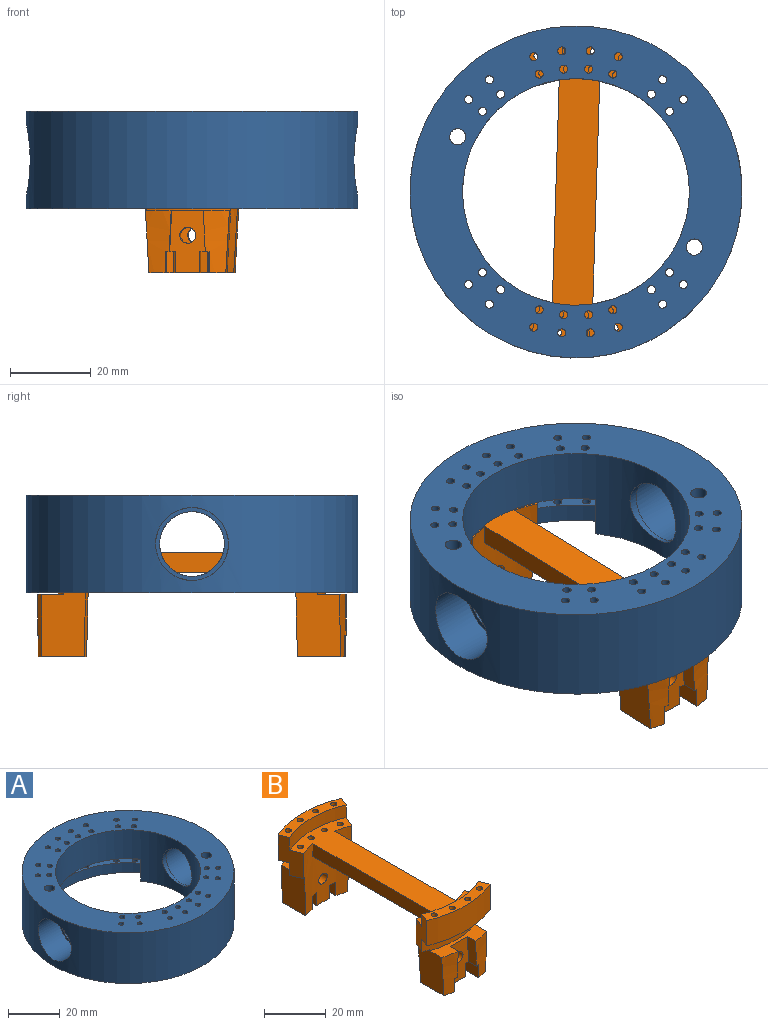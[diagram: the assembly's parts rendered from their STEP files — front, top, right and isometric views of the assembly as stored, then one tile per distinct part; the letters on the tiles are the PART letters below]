
ASSEMBLY  parts=2 mates=1
PART A: 80 faces, bbox 82x82x24 mm
  f0: plane 82x82mm, normal (0,0,-1), area 1952.1mm2, adj f9,f11,f14,f15,f22,f24,f26,f28
  f1: plane 82x82mm, normal (0,0,1), area 2692.3mm2, adj f9,f11,f12,f13,f40,f41,f42,f43
  f2: plane 53.41x16.54mm, normal (0,0,-1), area 242.5mm2, adj f9,f21,f22,f24,f72,f73,f74,f75
  f3: plane 54.06x17.34mm, normal (0,0,-1), area 267.8mm2, adj f8,f9,f25,f26,f28,f29,f64,f65
  f4: plane 61.27x18.7mm, normal (0,0,-1), area 297.4mm2, adj f21,f22,f23,f24,f56,f57,f58,f59
  f5: plane 61.27x18.24mm, normal (0,0,1), area 246.7mm2, adj f22,f23,f24,f31,f48,f49,f50,f51
  f6: plane 61.27x18.7mm, normal (0,0,-1), area 272.1mm2, adj f8,f25,f26,f27,f28,f29,f40,f41
  f7: plane 61.27x18.24mm, normal (0,0,1), area 246.7mm2, adj f26,f27,f28,f30,f32,f33,f34,f35
  f8: cylinder r=33.4mm len=27.36mm, axis (0,0,-1), area 160.3mm2, adj f3,f6,f25,f26
  f9: cylinder r=28mm len=56mm, axis (0,0,-1), area 2687.3mm2, adj f0,f1,f2,f3,f10,f14,f15,f16
  f10: cylinder r=8mm len=16mm, axis (-1,0,0), area 79.4mm2, adj f9,f18
  f11: cylinder r=41mm len=82mm, axis (0,0,-1), area 5671.2mm2, adj f0,f1,f17,f19
  f12: cylinder r=2mm len=20.5mm, axis (0,0,-1), area 257.6mm2, adj f1,f14
  f13: cylinder r=2mm len=20.5mm, axis (0,0,-1), area 257.6mm2, adj f1,f15
  f14: cone r=5.5mm half-angle=45deg, axis (0,0,-1), area 108.8mm2, adj f0,f9,f12
  f15: cone r=2mm half-angle=45deg, axis (0,0,-1), area 108.8mm2, adj f0,f9,f13
  f16: cylinder r=8mm len=16mm, axis (-1,0,0), area 79.5mm2, adj f9,f20
  f17: cylinder r=9mm len=18mm, axis (-1,0,0), area 650.4mm2, adj f11,f18
  f18: plane 18x18mm, normal (1,0,0), area 53.4mm2, adj f10,f17
  f19: cylinder r=9mm len=18mm, axis (1,0,0), area 650.4mm2, adj f11,f20
  f20: plane 18x18mm, normal (-1,0,0), area 53.4mm2, adj f16,f19
  f21: cylinder r=32.6mm len=53.41mm, axis (0,0,-1), area 312.9mm2, adj f2,f4,f22,f24
  f22: plane 15.4x7.7mm, normal (-0.57,0.82,0), area 103.4mm2, adj f0,f2,f4,f5,f9,f21,f23,f31
  f23: cylinder r=37.4mm len=61.27mm, axis (0,0,-1), area 775.5mm2, adj f4,f5,f22,f24
  f24: plane 15.4x7.7mm, normal (0.57,0.82,0), area 103.4mm2, adj f0,f2,f4,f5,f9,f21,f23,f31
  f25: plane 5x0.8mm, normal (1,0,0), area 4mm2, adj f3,f6,f8,f29
  f26: plane 15.4x7.7mm, normal (0.57,-0.82,0), area 99.4mm2, adj f0,f3,f6,f7,f8,f9,f27,f30
  f27: cylinder r=37.4mm len=61.27mm, axis (0,0,-1), area 775.5mm2, adj f6,f7,f26,f28
  f28: plane 15.4x7.7mm, normal (-0.57,-0.82,0), area 103.4mm2, adj f0,f3,f6,f7,f9,f27,f29,f30
  f29: cylinder r=32.6mm len=26.7mm, axis (0,0,-1), area 156.5mm2, adj f3,f6,f25,f28
  f30: cylinder r=33.4mm len=54.72mm, axis (0,0,-1), area 295mm2, adj f0,f7,f26,f28
  f31: cylinder r=33.4mm len=54.72mm, axis (0,0,-1), area 295mm2, adj f0,f5,f22,f24
  f32: cylinder r=1mm len=4.6mm, axis (0,0,-1), area 28.9mm2, adj f0,f7
  f33: cylinder r=1mm len=4.6mm, axis (0,0,-1), area 28.9mm2, adj f0,f7
  f34: cylinder r=1mm len=4.6mm, axis (0,0,-1), area 28.9mm2, adj f0,f7
  f35: cylinder r=1mm len=4.6mm, axis (0,0,-1), area 28.9mm2, adj f0,f7
  f36: cylinder r=1mm len=4.6mm, axis (0,0,-1), area 28.9mm2, adj f0,f7
  f37: cylinder r=1mm len=4.6mm, axis (0,0,-1), area 28.9mm2, adj f0,f7
  f38: cylinder r=1mm len=4.6mm, axis (0,0,-1), area 28.9mm2, adj f0,f7
  f39: cylinder r=1mm len=4.6mm, axis (0,0,-1), area 28.9mm2, adj f0,f7
  f40: cylinder r=1mm len=8.6mm, axis (0,0,-1), area 54mm2, adj f1,f6
  f41: cylinder r=1mm len=8.6mm, axis (0,0,-1), area 54mm2, adj f1,f6
  f42: cylinder r=1mm len=8.6mm, axis (0,0,-1), area 54mm2, adj f1,f6
  f43: cylinder r=1mm len=8.6mm, axis (0,0,-1), area 54mm2, adj f1,f6
  f44: cylinder r=1mm len=8.6mm, axis (0,0,-1), area 54mm2, adj f1,f6
  f45: cylinder r=1mm len=8.6mm, axis (0,0,-1), area 54mm2, adj f1,f6
  f46: cylinder r=1mm len=8.6mm, axis (0,0,-1), area 54mm2, adj f1,f6
  f47: cylinder r=1mm len=8.6mm, axis (0,0,-1), area 54mm2, adj f1,f6
  f48: cylinder r=1mm len=4.6mm, axis (0,0,-1), area 28.9mm2, adj f0,f5
  f49: cylinder r=1mm len=4.6mm, axis (0,0,-1), area 28.9mm2, adj f0,f5
  f50: cylinder r=1mm len=4.6mm, axis (0,0,-1), area 28.9mm2, adj f0,f5
  f51: cylinder r=1mm len=4.6mm, axis (0,0,-1), area 28.9mm2, adj f0,f5
  f52: cylinder r=1mm len=4.6mm, axis (0,0,-1), area 28.9mm2, adj f0,f5
  f53: cylinder r=1mm len=4.6mm, axis (0,0,-1), area 28.9mm2, adj f0,f5
  f54: cylinder r=1mm len=4.6mm, axis (0,0,-1), area 28.9mm2, adj f0,f5
  f55: cylinder r=1mm len=4.6mm, axis (0,0,-1), area 28.9mm2, adj f0,f5
  f56: cylinder r=1mm len=8.6mm, axis (0,0,-1), area 54mm2, adj f1,f4
  f57: cylinder r=1mm len=8.6mm, axis (0,0,-1), area 54mm2, adj f1,f4
  f58: cylinder r=1mm len=8.6mm, axis (0,0,-1), area 54mm2, adj f1,f4
  f59: cylinder r=1mm len=8.6mm, axis (0,0,-1), area 54mm2, adj f1,f4
  f60: cylinder r=1mm len=8.6mm, axis (0,0,-1), area 54mm2, adj f1,f4
  f61: cylinder r=1mm len=8.6mm, axis (0,0,-1), area 54mm2, adj f1,f4
  f62: cylinder r=1mm len=8.6mm, axis (0,0,-1), area 54mm2, adj f1,f4
  f63: cylinder r=1mm len=8.6mm, axis (0,0,-1), area 54mm2, adj f1,f4
  f64: cylinder r=1mm len=13.6mm, axis (0,0,-1), area 85.5mm2, adj f1,f3
  f65: cylinder r=1mm len=13.6mm, axis (0,0,-1), area 85.5mm2, adj f1,f3
  f66: cylinder r=1mm len=13.6mm, axis (0,0,-1), area 85.5mm2, adj f1,f3
  f67: cylinder r=1mm len=13.6mm, axis (0,0,-1), area 85.5mm2, adj f1,f3
  f68: cylinder r=1mm len=13.6mm, axis (0,0,-1), area 85.5mm2, adj f1,f3
  f69: cylinder r=1mm len=13.6mm, axis (0,0,-1), area 85.5mm2, adj f1,f3
  f70: cylinder r=1mm len=13.6mm, axis (0,0,-1), area 85.5mm2, adj f1,f3
  f71: cylinder r=1mm len=13.6mm, axis (0,0,-1), area 85.5mm2, adj f1,f3
  f72: cylinder r=1mm len=13.6mm, axis (0,0,-1), area 85.5mm2, adj f1,f2
  f73: cylinder r=1mm len=13.6mm, axis (0,0,-1), area 85.5mm2, adj f1,f2
  f74: cylinder r=1mm len=13.6mm, axis (0,0,-1), area 85.5mm2, adj f1,f2
  f75: cylinder r=1mm len=13.6mm, axis (0,0,-1), area 85.5mm2, adj f1,f2
  f76: cylinder r=1mm len=13.6mm, axis (0,0,-1), area 85.5mm2, adj f1,f2
  f77: cylinder r=1mm len=13.6mm, axis (0,0,-1), area 85.5mm2, adj f1,f2
  f78: cylinder r=1mm len=13.6mm, axis (0,0,-1), area 85.5mm2, adj f1,f2
  f79: cylinder r=1mm len=13.6mm, axis (0,0,-1), area 85.5mm2, adj f1,f2
PART B: 84 faces, bbox 29.1x76x30.8 mm
  f0: cylinder r=28mm len=25.8mm, axis (0,0,1), area 459.5mm2, adj f3,f4,f7,f8,f9,f12,f16,f17
  f1: plane 29.07x6.65mm, normal (0,0,1), area 100.5mm2, adj f4,f12,f27,f28,f37,f38,f39,f40
  f2: plane 29.07x6.65mm, normal (0,0,-1), area 100.5mm2, adj f4,f10,f12,f27,f37,f38,f39,f40
  f3: plane 66x25.93mm, normal (0,0,1), area 778.2mm2, adj f0,f4,f12,f28,f29,f31,f33,f35
  f4: plane 15x8.28mm, normal (-0.92,0.39,0), area 90mm2, adj f0,f1,f2,f3,f10,f18,f27,f28
  f5: plane 20.75x6.67mm, normal (0,0,1), area 78.7mm2, adj f6,f10,f11,f13,f14,f15,f17,f19
  f6: cylinder r=38.2mm len=15.4mm, axis (0,0,1), area 83.4mm2, adj f5,f7,f14,f19,f21,f22
  f7: plane 11.47x4.05mm, normal (0,0,-1), area 42.5mm2, adj f0,f6,f19,f22
  f8: plane 11.47x4.05mm, normal (0,0,-1), area 42.5mm2, adj f0,f11,f17,f25
  f9: plane 6.41x6mm, normal (0,0,-1), area 37.8mm2, adj f0,f15,f20,f23
  f10: cylinder r=33mm len=25.93mm, axis (0,0,1), area 141.7mm2, adj f2,f4,f5,f12,f16,f17,f18,f19
  f11: cylinder r=38.2mm len=15.4mm, axis (0,0,1), area 83.4mm2, adj f5,f8,f13,f17,f24,f25
  f12: plane 15x8.28mm, normal (0.92,0.39,0), area 90mm2, adj f0,f1,f2,f3,f10,f16,f27,f28
  f13: plane 10.2x3.75mm, normal (-1,0,-0.05), area 38mm2, adj f5,f11,f15,f24
  f14: plane 10.2x3.75mm, normal (1,0,-0.05), area 38mm2, adj f5,f6,f15,f21
  f15: plane 15.4x8.9mm, normal (0,-1,0), area 105.1mm2, adj f5,f9,f13,f14,f20,f21,f23,f24
  f16: plane 5.57x2.56mm, normal (0,0,-1), area 8.5mm2, adj f0,f10,f12,f17
  f17: plane 15.82x11.03mm, normal (1,0,-0.06), area 167.3mm2, adj f0,f5,f8,f10,f11,f16
  f18: plane 5.57x2.56mm, normal (0,0,-1), area 8.5mm2, adj f0,f4,f10,f19
  f19: plane 15.82x11.03mm, normal (-1,0,-0.06), area 167.3mm2, adj f0,f5,f6,f7,f10,f18
  f20: plane 6.41x5.2mm, normal (-1,0,0), area 33.3mm2, adj f0,f9,f15,f21
  f21: plane 10.48x2.45mm, normal (0,0,-1), area 19.7mm2, adj f0,f6,f14,f15,f20,f22
  f22: plane 10.34x5.2mm, normal (1,0,0), area 53.8mm2, adj f0,f6,f7,f21
  f23: plane 6.41x5.2mm, normal (1,0,0), area 33.3mm2, adj f0,f9,f15,f24
  f24: plane 10.48x2.45mm, normal (0,0,-1), area 19.7mm2, adj f0,f11,f13,f15,f23,f25
  f25: plane 10.34x5.2mm, normal (-1,0,0), area 53.8mm2, adj f0,f8,f11,f24
  f26: cylinder r=1.95mm len=6.32mm, axis (0,1,0), area 77mm2, adj f0,f15
  f27: cylinder r=37mm len=29.07mm, axis (0,0,-1), area 298.8mm2, adj f1,f2,f4,f12
  f28: cylinder r=33mm len=25.93mm, axis (0,0,-1), area 133.2mm2, adj f1,f3,f4,f12
  f29: cylinder r=1mm len=10mm, axis (0,0,-1), area 62.8mm2, adj f3,f30
  f30: plane 2x2mm, normal (0,0,1), area 3.1mm2, adj f29
  f31: cylinder r=1mm len=10mm, axis (0,0,-1), area 62.8mm2, adj f3,f32
  f32: plane 2x2mm, normal (0,0,1), area 3.1mm2, adj f31
  f33: cylinder r=1mm len=10mm, axis (0,0,-1), area 62.8mm2, adj f3,f34
  f34: plane 2x2mm, normal (0,0,1), area 3.1mm2, adj f33
  f35: cylinder r=1mm len=10mm, axis (0,0,-1), area 62.8mm2, adj f3,f36
  f36: plane 2x2mm, normal (0,0,1), area 3.1mm2, adj f35
  f37: cylinder r=1mm len=10mm, axis (0,0,-1), area 62.8mm2, adj f1,f2
  f38: cylinder r=1mm len=10mm, axis (0,0,-1), area 62.8mm2, adj f1,f2
  f39: cylinder r=1mm len=10mm, axis (0,0,-1), area 62.8mm2, adj f1,f2
  f40: cylinder r=1mm len=10mm, axis (0,0,-1), area 62.8mm2, adj f1,f2
  f41: plane 55.1x5mm, normal (-1,0,0), area 275.5mm2, adj f0,f3,f43,f44
  f42: plane 55.1x5mm, normal (1,0,0), area 275.5mm2, adj f0,f3,f43,f44
  f43: plane 56x10mm, normal (0,0,-1), area 557mm2, adj f0,f41,f42,f44
  f44: cylinder r=28mm len=25.8mm, axis (0,0,1), area 459.5mm2, adj f3,f41,f42,f43,f47,f50,f51,f52
  f45: plane 29.07x6.65mm, normal (0,0,1), area 100.5mm2, adj f47,f55,f70,f71,f80,f81,f82,f83
  f46: plane 29.07x6.65mm, normal (0,0,-1), area 100.5mm2, adj f47,f53,f55,f70,f80,f81,f82,f83
  f47: plane 15x8.28mm, normal (-0.92,-0.39,0), area 90mm2, adj f3,f44,f45,f46,f53,f61,f70,f71
  f48: plane 20.75x6.67mm, normal (0,0,1), area 78.7mm2, adj f49,f53,f54,f56,f57,f58,f60,f62
  f49: cylinder r=38.2mm len=15.4mm, axis (0,0,1), area 83.4mm2, adj f48,f50,f57,f62,f64,f65
  f50: plane 11.47x4.05mm, normal (0,0,-1), area 42.5mm2, adj f44,f49,f62,f65
  f51: plane 11.47x4.05mm, normal (0,0,-1), area 42.5mm2, adj f44,f54,f60,f68
  f52: plane 6.41x6mm, normal (0,0,-1), area 37.8mm2, adj f44,f58,f63,f66
  f53: cylinder r=33mm len=25.93mm, axis (0,0,1), area 141.7mm2, adj f46,f47,f48,f55,f59,f60,f61,f62
  f54: cylinder r=38.2mm len=15.4mm, axis (0,0,1), area 83.4mm2, adj f48,f51,f56,f60,f67,f68
  f55: plane 15x8.28mm, normal (0.92,-0.39,0), area 90mm2, adj f3,f44,f45,f46,f53,f59,f70,f71
  f56: plane 10.2x3.75mm, normal (-1,0,-0.05), area 38mm2, adj f48,f54,f58,f67
  f57: plane 10.2x3.75mm, normal (1,0,-0.05), area 38mm2, adj f48,f49,f58,f64
  f58: plane 15.4x8.9mm, normal (0,1,0), area 105.1mm2, adj f48,f52,f56,f57,f63,f64,f66,f67
  f59: plane 5.57x2.56mm, normal (0,0,-1), area 8.5mm2, adj f44,f53,f55,f60
  f60: plane 15.82x11.03mm, normal (1,0,-0.06), area 167.3mm2, adj f44,f48,f51,f53,f54,f59
  f61: plane 5.57x2.56mm, normal (0,0,-1), area 8.5mm2, adj f44,f47,f53,f62
  f62: plane 15.82x11.03mm, normal (-1,0,-0.06), area 167.3mm2, adj f44,f48,f49,f50,f53,f61
  f63: plane 6.41x5.2mm, normal (-1,0,0), area 33.3mm2, adj f44,f52,f58,f64
  f64: plane 10.48x2.45mm, normal (0,0,-1), area 19.7mm2, adj f44,f49,f57,f58,f63,f65
  f65: plane 10.34x5.2mm, normal (1,0,0), area 53.8mm2, adj f44,f49,f50,f64
  f66: plane 6.41x5.2mm, normal (1,0,0), area 33.3mm2, adj f44,f52,f58,f67
  f67: plane 10.48x2.45mm, normal (0,0,-1), area 19.7mm2, adj f44,f54,f56,f58,f66,f68
  f68: plane 10.34x5.2mm, normal (-1,0,0), area 53.8mm2, adj f44,f51,f54,f67
  f69: cylinder r=1.95mm len=6.32mm, axis (0,-1,0), area 77mm2, adj f44,f58
  f70: cylinder r=37mm len=29.07mm, axis (0,0,-1), area 298.8mm2, adj f45,f46,f47,f55
  f71: cylinder r=33mm len=25.93mm, axis (0,0,-1), area 133.2mm2, adj f3,f45,f47,f55
  f72: cylinder r=1mm len=10mm, axis (0,0,-1), area 62.8mm2, adj f3,f73
  f73: plane 2x2mm, normal (0,0,1), area 3.1mm2, adj f72
  f74: cylinder r=1mm len=10mm, axis (0,0,-1), area 62.8mm2, adj f3,f75
  f75: plane 2x2mm, normal (0,0,1), area 3.1mm2, adj f74
  f76: cylinder r=1mm len=10mm, axis (0,0,-1), area 62.8mm2, adj f3,f77
  f77: plane 2x2mm, normal (0,0,1), area 3.1mm2, adj f76
  f78: cylinder r=1mm len=10mm, axis (0,0,-1), area 62.8mm2, adj f3,f79
  f79: plane 2x2mm, normal (0,0,1), area 3.1mm2, adj f78
  f80: cylinder r=1mm len=10mm, axis (0,0,-1), area 62.8mm2, adj f45,f46
  f81: cylinder r=1mm len=10mm, axis (0,0,-1), area 62.8mm2, adj f45,f46
  f82: cylinder r=1mm len=10mm, axis (0,0,-1), area 62.8mm2, adj f45,f46
  f83: cylinder r=1mm len=10mm, axis (0,0,-1), area 62.8mm2, adj f45,f46
PLACE A t=(0,0,-24)mm
PLACE B rot(axis=(0,0,-1),1.8deg) t=(0,0,-24)mm
MATE revolute B.f6 <-> A.f8  axis (0,0,1) through (0,0,-24)mm
